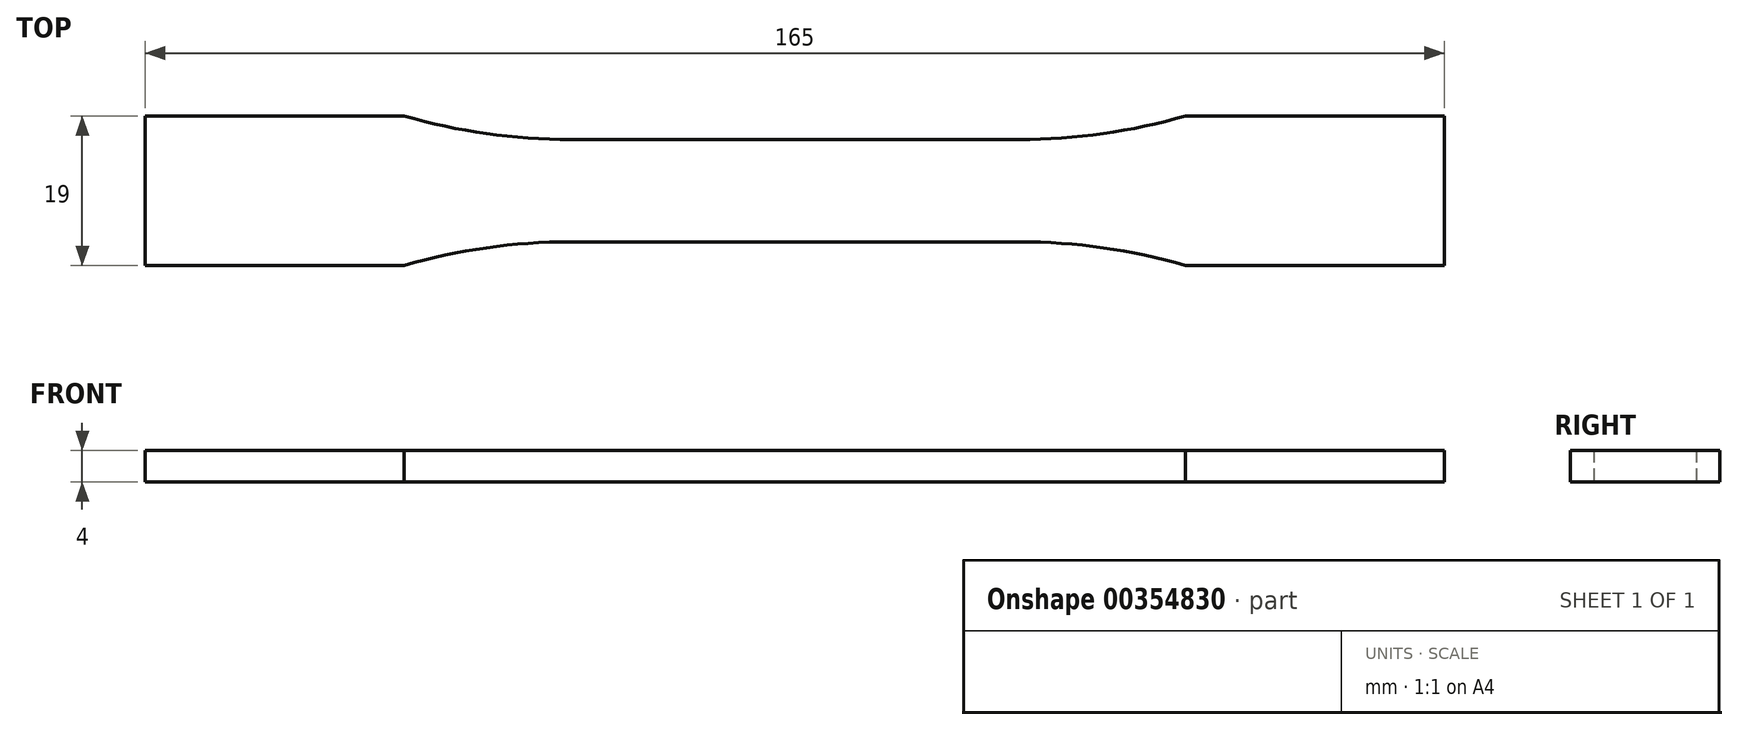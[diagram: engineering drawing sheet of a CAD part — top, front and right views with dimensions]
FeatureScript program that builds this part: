
annotation { "Feature Type Name" : "Feature", "Feature Type Description" : "" }
export const myFeature = defineFeature(function(context is Context, id is Id, definition is map)
    precondition{}
    {
        {
            var Q0;
            Q0=qCreatedBy(makeId("Top.planeOp"),FACE);
            var sketch = newSketch(context, id + "F0", { "sketchPlane" : qUnion([Q0])});
            skLineSegment(sketch, "E0.bottom", {"start": v(-28.5, 6.5) * mm, "end": v(28.5, 6.5) * mm});
            skLineSegment(sketch, "E0.top", {"start": v(-28.5, -6.5) * mm, "end": v(28.5, -6.5) * mm});
            skPoint(sketch, "E0.middle", {"position": v(0, 0) * mm});
            skLineSegment(sketch, "E1.bottom", {"start": v(-49.64, -9.5) * mm, "end": v(-82.5, -9.5) * mm});
            skLineSegment(sketch, "E1.top", {"start": v(-49.64, 9.5) * mm, "end": v(-82.5, 9.5) * mm});
            skLineSegment(sketch, "E1.right", {"start": v(-82.5, -9.5) * mm, "end": v(-82.5, 9.5) * mm});
            skLineSegment(sketch, "E2.bottom", {"start": v(49.64, -9.5) * mm, "end": v(82.5, -9.5) * mm});
            skLineSegment(sketch, "E2.top", {"start": v(49.64, 9.5) * mm, "end": v(82.5, 9.5) * mm});
            skLineSegment(sketch, "E2.right", {"start": v(82.5, -9.5) * mm, "end": v(82.5, 9.5) * mm});
            skLineSegment(sketch, "E3", {"start": v(0, 0) * mm, "end": v(-20.4, 0) * mm});
            skLineSegment(sketch, "E4", {"start": v(0, 0) * mm, "end": v(0, 3.9) * mm});
            skArc(sketch, "E5", {"start": v(-49.64, 9.5) * mm, "mid": v(-39.18, 7.25) * mm, "end": v(-28.5, 6.5) * mm});
            skArc(sketch, "E6", {"start": v(-28.5, -6.5) * mm, "mid": v(-39.18, -7.25) * mm, "end": v(-49.64, -9.5) * mm});
            skArc(sketch, "E7.MirrorCS", {"start": v(49.64, 9.5) * mm, "mid": v(39.18, 7.25) * mm, "end": v(28.5, 6.5) * mm});
            skArc(sketch, "E8.MirrorCS", {"start": v(28.5, -6.5) * mm, "mid": v(39.18, -7.25) * mm, "end": v(49.64, -9.5) * mm});
            skSolve(sketch);
        }
        {
            var Q0;
            Q0 = qSketchRegion(id + "F0", true);
            extrude(context, id + "F1", {"entities" : qUnion([Q0]), "depth" : 4 * mm, "offsetDistance" : 25 * mm});
        }
    });
